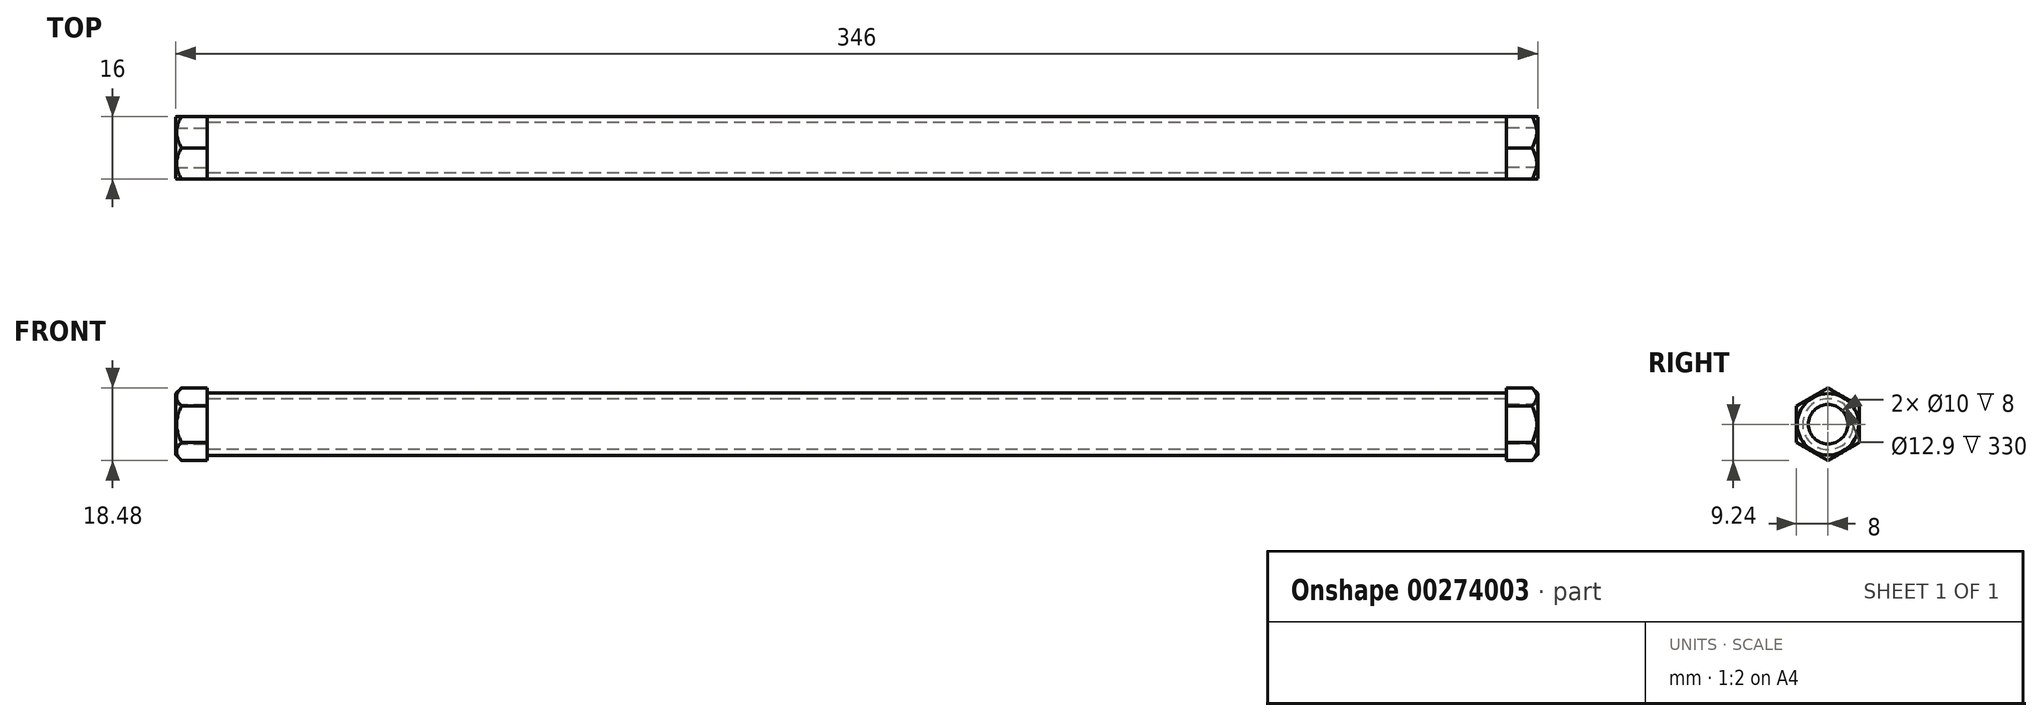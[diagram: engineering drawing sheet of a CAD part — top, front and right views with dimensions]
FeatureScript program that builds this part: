
annotation { "Feature Type Name" : "Feature", "Feature Type Description" : "" }
export const myFeature = defineFeature(function(context is Context, id is Id, definition is map)
    precondition{}
    {
        {
            var Q0;
            Q0=qCreatedBy(makeId("Right.planeOp"),FACE);
            var sketch = newSketch(context, id + "F0", { "sketchPlane" : qUnion([Q0])});
            skCircle(sketch, "E0", {"center": v(0, 0) * mm, "radius": 7.95 * mm});
            skCircle(sketch, "E1", {"center": v(0, 0) * mm, "radius": 6.45 * mm});
            skSolve(sketch);
        }
        {
            var Q0;
            Q0=qSketchRegion(id+"F0",true);
            extrude(context, id + "F1", {"entities" : qUnion([Q0]), "endBound" : BoundingType.SYMMETRIC, "depth" : 330 * mm});
        }
        {
            var Q0;
            Q0=makeQuery(id+"F1.opExtrude","CAP_FACE",FACE,{"disambiguationData":[OSD([sQuery(id+"F0.wireOp",EDGE,"E0"),sQuery(id+"F0.wireOp",EDGE,"E1")])],"isStart":false});
            var sketch = newSketch(context, id + "F2", { "sketchPlane" : qUnion([Q0])});
            skCircle(sketch, "E2", {"center": v(0, 0) * mm, "radius": 5 * mm});
            skCircle(sketch, "E3.cCircle", {"center": v(0, 0) * mm, "radius": 8 * mm, "construction": true});
            skLineSegment(sketch, "E3.0", {"start": v(8, 4.62) * mm, "end": v(8, -4.62) * mm});
            skLineSegment(sketch, "E3.1", {"start": v(8, -4.62) * mm, "end": v(0, -9.24) * mm});
            skLineSegment(sketch, "E3.2", {"start": v(0, -9.24) * mm, "end": v(-8, -4.62) * mm});
            skLineSegment(sketch, "E3.3", {"start": v(-8, -4.62) * mm, "end": v(-8, 4.62) * mm});
            skLineSegment(sketch, "E3.4", {"start": v(-8, 4.62) * mm, "end": v(0, 9.24) * mm});
            skLineSegment(sketch, "E3.5", {"start": v(0, 9.24) * mm, "end": v(8, 4.62) * mm});
            skPoint(sketch, "E3.0.midPoint", {"position": v(8, 0) * mm});
            skSolve(sketch);
        }
        {
            var Q0;
            Q0=qSketchRegion(id+"F2",true);
            extrude(context, id + "F3", {"entities" : qUnion([Q0]), "depth" : 8 * mm});
        }
        {
            var Q0;
            Q0=qCreatedBy(makeId("Front.planeOp"),FACE);
            var sketch = newSketch(context, id + "F4", { "sketchPlane" : qUnion([Q0])});
            skPoint(sketch, "E4.0", {"position": v(173, 9.24) * mm});
            skLineSegment(sketch, "E5", {"start": v(173, 9.24) * mm, "end": v(171.55, 9.24) * mm});
            skLineSegment(sketch, "E6", {"start": v(171.55, 9.24) * mm, "end": v(173, 7.79) * mm});
            skLineSegment(sketch, "E7", {"start": v(173, 7.79) * mm, "end": v(173, 9.24) * mm});
            skLineSegment(sketch, "E8", {"start": v(0, 0) * mm, "end": v(232.31, 0) * mm, "construction": true});
            skSolve(sketch);
        }
        {
            var Q0;
            Q0=qSketchRegion(id+"F4",true);
            var Q1;
            Q1=sQuery(id+"F4.wireOp",EDGE,"E8");
            revolve(context, id + "F5", {"operationType" : NewBodyOperationType.REMOVE, "entities" : qUnion([Q0]), "axis" : qUnion([Q1]), "revolveType" : RevolveType.FULL, "oppositeDirection" : true});
        }
        {
            var Q0;
            Q0=makeQuery(id+"F3.opExtrude","SWEPT_BODY",BODY,{"disambiguationData":[OSD([sQuery(id+"F2.wireOp",EDGE,"E2"),sQuery(id+"F2.wireOp",EDGE,"E3.0"),sQuery(id+"F2.wireOp",EDGE,"E3.1"),sQuery(id+"F2.wireOp",EDGE,"E3.2"),sQuery(id+"F2.wireOp",EDGE,"E3.3"),sQuery(id+"F2.wireOp",EDGE,"E3.4"),sQuery(id+"F2.wireOp",EDGE,"E3.5")])]});
            var Q1;
            Q1=qCreatedBy(makeId("Right.planeOp"),FACE);
            mirror(context, id + "F6", {"entities" : qUnion([Q0]), "mirrorPlane" : qUnion([Q1])});
        }
    });
